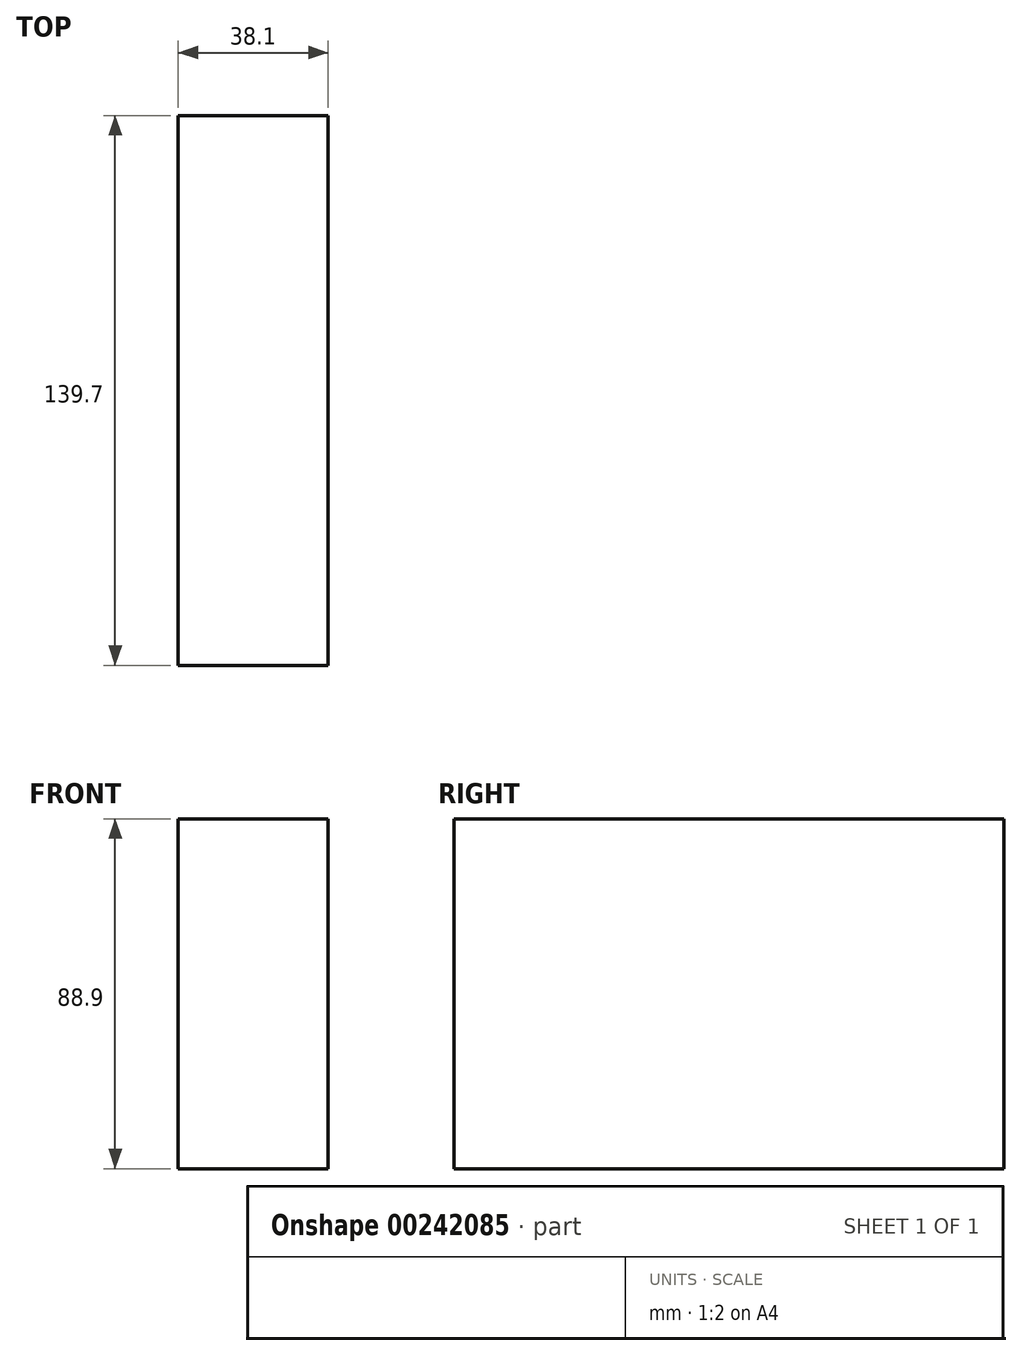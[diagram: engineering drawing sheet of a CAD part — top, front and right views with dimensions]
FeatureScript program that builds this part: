
annotation { "Feature Type Name" : "Feature", "Feature Type Description" : "" }
export const myFeature = defineFeature(function(context is Context, id is Id, definition is map)
    precondition{}
    {
        {
            var Q0;
            Q0=qCreatedBy(makeId("Front.planeOp"),FACE);
            var sketch = newSketch(context, id + "F0", { "sketchPlane" : qUnion([Q0])});
            skLineSegment(sketch, "E0.bottom", {"start": v(-38.1, 88.9) * mm, "end": v(0, 88.9) * mm});
            skLineSegment(sketch, "E0.top", {"start": v(-38.1, 0) * mm, "end": v(0, 0) * mm});
            skLineSegment(sketch, "E0.left", {"start": v(-38.1, 88.9) * mm, "end": v(-38.1, 0) * mm});
            skLineSegment(sketch, "E0.right", {"start": v(0, 88.9) * mm, "end": v(0, 0) * mm});
            skSolve(sketch);
        }
        {
            var Q0;
            Q0=makeQuery(id+"F0.imprint","IMPRINT",FACE,{"disambiguationData":[TD([[makeQuery(id+"F0.imprint","IMPRINT",EDGE,{"derivedFrom":sQuery(id+"F0.wireOp",EDGE,"E0.bottom")}),-1.0]])]});
            extrude(context, id + "F1", {"entities" : qUnion([Q0]), "depth" : 139.7 * mm});
        }
    });
